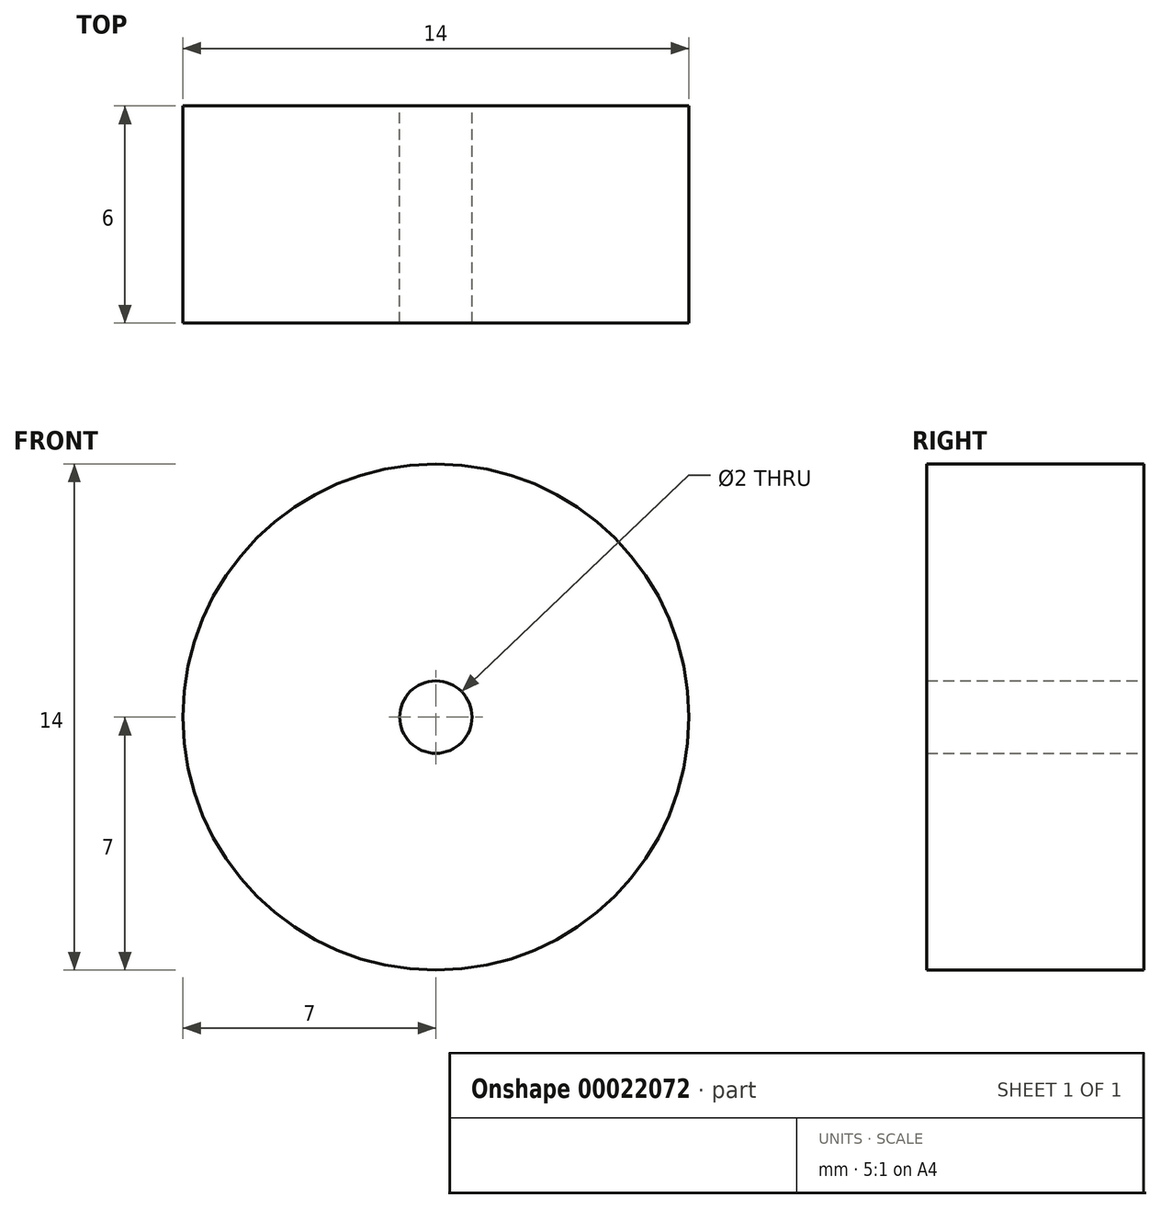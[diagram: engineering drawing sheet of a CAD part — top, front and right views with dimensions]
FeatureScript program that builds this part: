
annotation { "Feature Type Name" : "Feature", "Feature Type Description" : "" }
export const myFeature = defineFeature(function(context is Context, id is Id, definition is map)
    precondition{}
    {
        {
            var Q0;
            Q0=qCreatedBy(makeId("Front.planeOp"),FACE);
            var sketch = newSketch(context, id + "F0", { "sketchPlane" : qUnion([Q0])});
            skCircle(sketch, "E0", {"center": v(0, 0) * mm, "radius": 7 * mm});
            skCircle(sketch, "E1", {"center": v(0, 0) * mm, "radius": 4.5 * mm});
            skCircle(sketch, "E2", {"center": v(0, 0) * mm, "radius": 1 * mm});
            skSolve(sketch);
        }
        {
            var Q0;
            Q0=makeQuery(id+"F0.imprint","IMPRINT",FACE,{"disambiguationData":[TD([[makeQuery(id+"F0.imprint","IMPRINT",EDGE,{"derivedFrom":sQuery(id+"F0.wireOp",EDGE,"E0")}),1.0]])]});
            extrude(context, id + "F1", {"entities" : qUnion([Q0]), "endBound" : BoundingType.SYMMETRIC, "depth" : 6 * mm});
        }
        {
            var Q0;
            Q0=makeQuery(id+"F0.imprint","IMPRINT",FACE,{"disambiguationData":[TD([[makeQuery(id+"F0.imprint","IMPRINT",EDGE,{"derivedFrom":sQuery(id+"F0.wireOp",EDGE,"E1")}),1.0]])]});
            extrude(context, id + "F2", {"entities" : qUnion([Q0]), "operationType" : NewBodyOperationType.ADD, "endBound" : BoundingType.SYMMETRIC, "depth" : 6 * mm});
        }
    });
